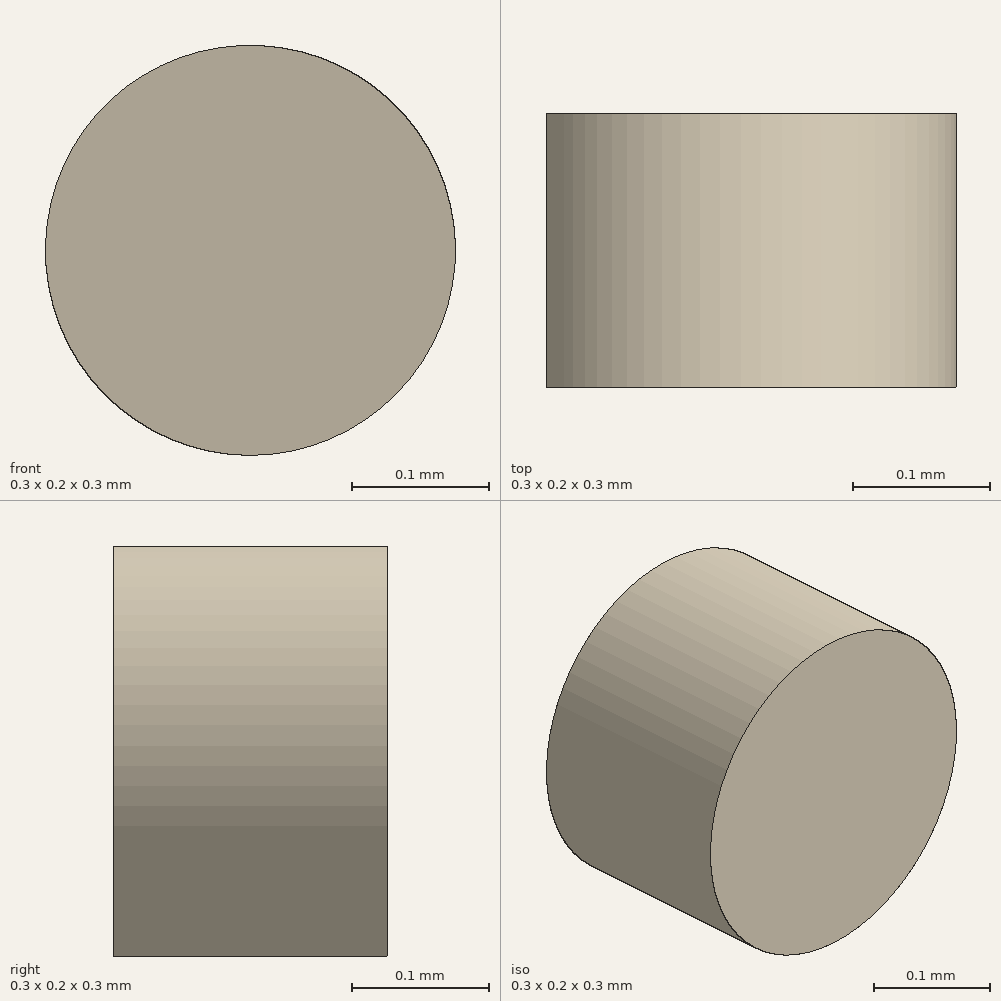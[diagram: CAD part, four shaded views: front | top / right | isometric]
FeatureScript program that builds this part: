
annotation { "Feature Type Name" : "Feature", "Feature Type Description" : "" }
export const myFeature = defineFeature(function(context is Context, id is Id, definition is map)
    precondition{}
    {
        {
            var Q0;
            Q0=qCreatedBy(makeId("Front.planeOp"),FACE);
            var sketch = newSketch(context, id + "F0", { "sketchPlane" : qUnion([Q0])});
            skCircle(sketch, "E0", {"center": v(0, 0) * mm, "radius": 0.15 * mm});
            skSolve(sketch);
        }
        {
            var Q0;
            Q0 = qSketchRegion(id + "F0", true);
            extrude(context, id + "F1", {"entities" : qUnion([Q0]), "depth" : 0.2 * mm});
        }
    });
